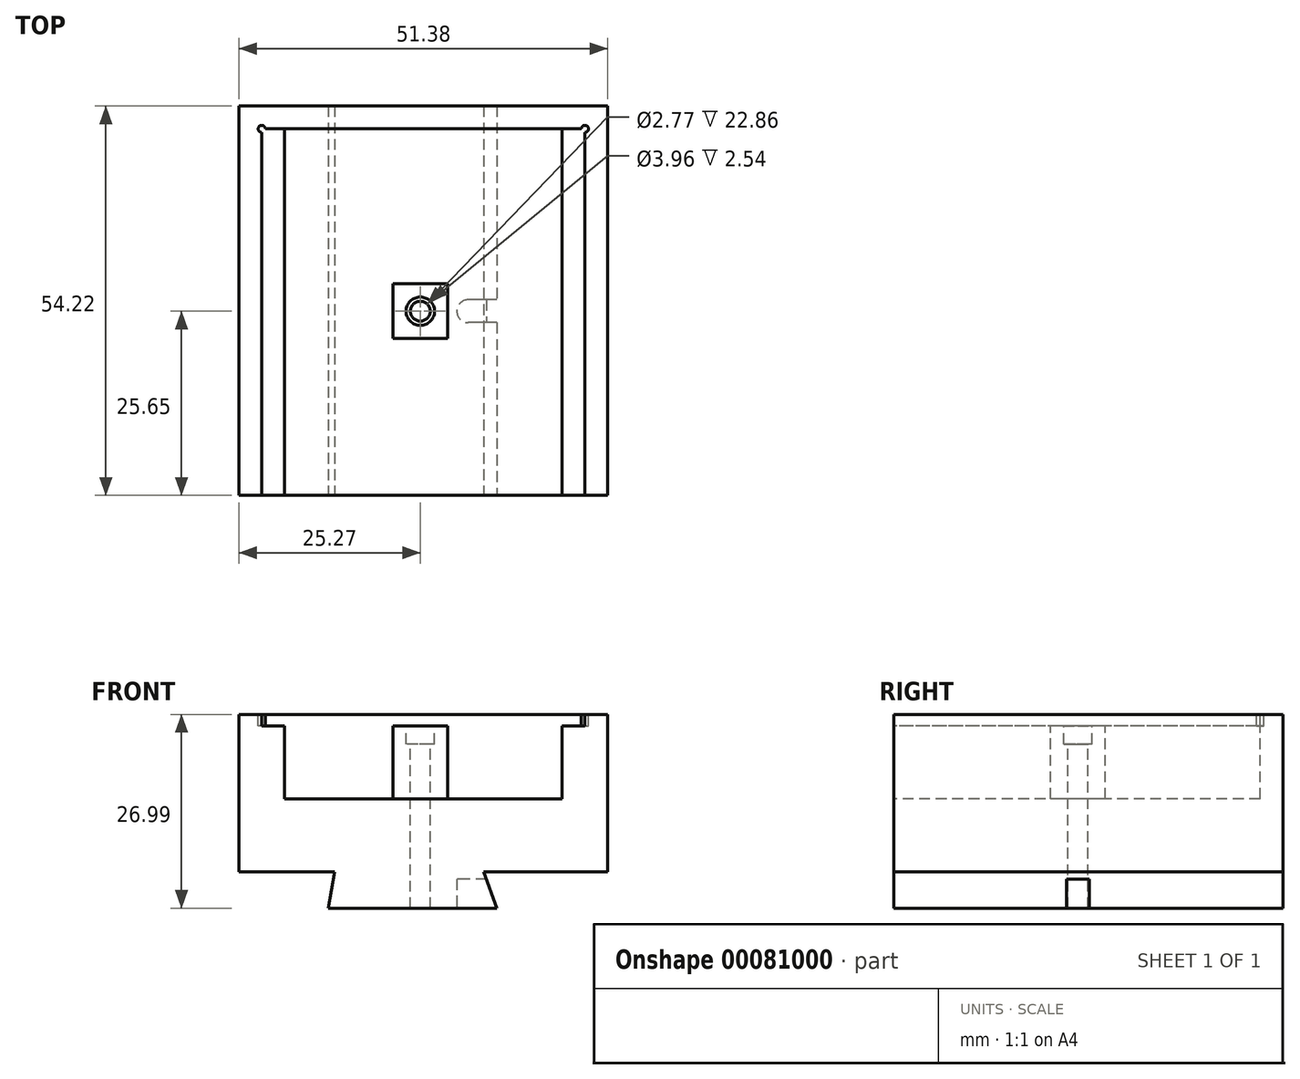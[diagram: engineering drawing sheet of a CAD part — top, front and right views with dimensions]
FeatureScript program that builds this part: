
annotation { "Feature Type Name" : "Feature", "Feature Type Description" : "" }
export const myFeature = defineFeature(function(context is Context, id is Id, definition is map)
    precondition{}
    {
        {
            var Q0;
            Q0=qCreatedBy(makeId("Top.planeOp"),FACE);
            var sketch = newSketch(context, id + "F0", { "sketchPlane" : qUnion([Q0])});
            skLineSegment(sketch, "E0.bottom", {"start": v(-25.27, 28.57) * mm, "end": v(26.11, 28.58) * mm});
            skLineSegment(sketch, "E0.top", {"start": v(-25.27, -25.65) * mm, "end": v(26.11, -25.65) * mm});
            skLineSegment(sketch, "E0.left", {"start": v(-25.27, 28.57) * mm, "end": v(-25.27, -25.65) * mm});
            skLineSegment(sketch, "E0.right", {"start": v(26.11, 28.58) * mm, "end": v(26.11, -25.65) * mm});
            skLineSegment(sketch, "E1.bottom", {"start": v(-22.1, 25.4) * mm, "end": v(22.94, 25.4) * mm});
            skLineSegment(sketch, "E1.top", {"start": v(-22.1, -25.65) * mm, "end": v(22.94, -25.65) * mm});
            skLineSegment(sketch, "E1.left", {"start": v(-22.1, 25.4) * mm, "end": v(-22.1, -25.65) * mm});
            skLineSegment(sketch, "E1.right", {"start": v(22.94, 25.4) * mm, "end": v(22.94, -25.65) * mm});
            skCircle(sketch, "E2", {"center": v(22.94, 25.4) * mm, "radius": 0.5 * mm});
            skCircle(sketch, "E3", {"center": v(-22.1, 25.4) * mm, "radius": 0.5 * mm});
            skCircle(sketch, "E4", {"center": v(0, 0) * mm, "radius": 1.38 * mm});
            skLineSegment(sketch, "E5", {"start": v(-18.92, 25.4) * mm, "end": v(-18.92, -25.65) * mm});
            skLineSegment(sketch, "E6", {"start": v(19.76, 25.4) * mm, "end": v(19.76, -25.65) * mm});
            skLineSegment(sketch, "E7.bottom", {"start": v(-3.8, 3.81) * mm, "end": v(3.81, 3.81) * mm});
            skLineSegment(sketch, "E7.top", {"start": v(-3.8, -3.81) * mm, "end": v(3.81, -3.81) * mm});
            skLineSegment(sketch, "E7.left", {"start": v(-3.81, 3.81) * mm, "end": v(-3.81, -3.81) * mm});
            skLineSegment(sketch, "E7.right", {"start": v(3.81, 3.81) * mm, "end": v(3.81, -3.81) * mm});
            skCircle(sketch, "E8", {"center": v(0, 0) * mm, "radius": 1.98 * mm});
            skSolve(sketch);
        }
        {
            var Q0;
            {var subQ5=sQuery(id+"F0.wireOp",EDGE,"E5");Q0=makeQuery(id+"F0.imprint","IMPRINT",FACE,{"disambiguationData":[TD([[makeQuery(id+"F0.imprint","IMPRINT",EDGE,{"derivedFrom":subQ5}),-1.0]])]});}
            var Q1;
            {var subQ0=sQuery(id+"F0.wireOp",EDGE,"E1.left");var subQ1=sQuery(id+"F0.wireOp",EDGE,"E1.bottom");var subQ2=makeQuery(id+"F0.imprint","INTERSECT",VERTEX,{"derivedFrom":[subQ1,subQ0]});Q1=makeQuery(id+"F0.imprint","IMPRINT",FACE,{"disambiguationData":[TD([[makeQuery(id+"F0.imprint","IMPRINT",EDGE,{"disambiguationData":[TD([[subQ2,-1.0]])],"derivedFrom":subQ1}),1.0]])]});}
            var Q2;
            {var subQ0=sQuery(id+"F0.wireOp",EDGE,"E1.left");var subQ1=sQuery(id+"F0.wireOp",EDGE,"E1.bottom");var subQ2=makeQuery(id+"F0.imprint","INTERSECT",VERTEX,{"derivedFrom":[subQ1,subQ0]});Q2=makeQuery(id+"F0.imprint","IMPRINT",FACE,{"disambiguationData":[TD([[makeQuery(id+"F0.imprint","IMPRINT",EDGE,{"disambiguationData":[TD([[subQ2,-1.0]])],"derivedFrom":subQ1}),-1.0]])]});}
            var Q3;
            {var subQ7=sQuery(id+"F0.wireOp",EDGE,"E6");Q3=makeQuery(id+"F0.imprint","IMPRINT",FACE,{"disambiguationData":[TD([[makeQuery(id+"F0.imprint","IMPRINT",EDGE,{"derivedFrom":subQ7}),1.0]])]});}
            var Q4;
            Q4=makeQuery(id+"F0.imprint","IMPRINT",FACE,{"disambiguationData":[TD([[makeQuery(id+"F0.imprint","IMPRINT",EDGE,{"derivedFrom":sQuery(id+"F0.wireOp",EDGE,"E4")}),-1.0]])]});
            var Q5;
            Q5=makeQuery(id+"F0.imprint","IMPRINT",FACE,{"disambiguationData":[TD([[makeQuery(id+"F0.imprint","IMPRINT",EDGE,{"derivedFrom":sQuery(id+"F0.wireOp",EDGE,"E0.bottom")}),-1.0]])]});
            var Q6;
            {var subQ0=sQuery(id+"F0.wireOp",EDGE,"E1.right");var subQ1=sQuery(id+"F0.wireOp",EDGE,"E1.bottom");var subQ2=makeQuery(id+"F0.imprint","INTERSECT",VERTEX,{"derivedFrom":[subQ1,subQ0]});Q6=makeQuery(id+"F0.imprint","IMPRINT",FACE,{"disambiguationData":[TD([[makeQuery(id+"F0.imprint","IMPRINT",EDGE,{"disambiguationData":[TD([[subQ2,1.0]])],"derivedFrom":subQ1}),-1.0]])]});}
            var Q7;
            {var subQ0=sQuery(id+"F0.wireOp",EDGE,"E1.right");var subQ1=sQuery(id+"F0.wireOp",EDGE,"E1.bottom");var subQ2=makeQuery(id+"F0.imprint","INTERSECT",VERTEX,{"derivedFrom":[subQ1,subQ0]});Q7=makeQuery(id+"F0.imprint","IMPRINT",FACE,{"disambiguationData":[TD([[makeQuery(id+"F0.imprint","IMPRINT",EDGE,{"disambiguationData":[TD([[subQ2,1.0]])],"derivedFrom":subQ1}),1.0]])]});}
            var Q8;
            {var subQ1=sQuery(id+"F0.wireOp",EDGE,"E5");Q8=makeQuery(id+"F0.imprint","IMPRINT",FACE,{"disambiguationData":[TD([[makeQuery(id+"F0.imprint","IMPRINT",EDGE,{"derivedFrom":subQ1}),1.0]])]});}
            var Q9;
            Q9=makeQuery(id+"F0.imprint","IMPRINT",FACE,{"disambiguationData":[TD([[makeQuery(id+"F0.imprint","IMPRINT",EDGE,{"derivedFrom":sQuery(id+"F0.wireOp",EDGE,"E7.bottom")}),-1.0]])]});
            extrude(context, id + "F1", {"entities" : qUnion([Q0, Q1, Q2, Q3, Q4, Q5, Q6, Q7, Q8, Q9]), "oppositeDirection" : true, "depth" : 26.99 * mm});
        }
        {
            var Q0;
            {var subQ5=sQuery(id+"F0.wireOp",EDGE,"E5");Q0=makeQuery(id+"F0.imprint","IMPRINT",FACE,{"disambiguationData":[TD([[makeQuery(id+"F0.imprint","IMPRINT",EDGE,{"derivedFrom":subQ5}),-1.0]])]});}
            var Q1;
            Q1=makeQuery(id+"F0.imprint","IMPRINT",FACE,{"disambiguationData":[TD([[makeQuery(id+"F0.imprint","IMPRINT",EDGE,{"derivedFrom":sQuery(id+"F0.wireOp",EDGE,"E4")}),-1.0]])]});
            var Q2;
            {var subQ7=sQuery(id+"F0.wireOp",EDGE,"E6");Q2=makeQuery(id+"F0.imprint","IMPRINT",FACE,{"disambiguationData":[TD([[makeQuery(id+"F0.imprint","IMPRINT",EDGE,{"derivedFrom":subQ7}),1.0]])]});}
            var Q3;
            {var subQ0=sQuery(id+"F0.wireOp",EDGE,"E1.right");var subQ1=sQuery(id+"F0.wireOp",EDGE,"E1.bottom");var subQ2=makeQuery(id+"F0.imprint","INTERSECT",VERTEX,{"derivedFrom":[subQ1,subQ0]});Q3=makeQuery(id+"F0.imprint","IMPRINT",FACE,{"disambiguationData":[TD([[makeQuery(id+"F0.imprint","IMPRINT",EDGE,{"disambiguationData":[TD([[subQ2,1.0]])],"derivedFrom":subQ1}),1.0]])]});}
            var Q4;
            {var subQ0=sQuery(id+"F0.wireOp",EDGE,"E1.right");var subQ1=sQuery(id+"F0.wireOp",EDGE,"E1.bottom");var subQ2=makeQuery(id+"F0.imprint","INTERSECT",VERTEX,{"derivedFrom":[subQ1,subQ0]});Q4=makeQuery(id+"F0.imprint","IMPRINT",FACE,{"disambiguationData":[TD([[makeQuery(id+"F0.imprint","IMPRINT",EDGE,{"disambiguationData":[TD([[subQ2,1.0]])],"derivedFrom":subQ1}),-1.0]])]});}
            var Q5;
            {var subQ0=sQuery(id+"F0.wireOp",EDGE,"E1.left");var subQ1=sQuery(id+"F0.wireOp",EDGE,"E1.bottom");var subQ2=makeQuery(id+"F0.imprint","INTERSECT",VERTEX,{"derivedFrom":[subQ1,subQ0]});Q5=makeQuery(id+"F0.imprint","IMPRINT",FACE,{"disambiguationData":[TD([[makeQuery(id+"F0.imprint","IMPRINT",EDGE,{"disambiguationData":[TD([[subQ2,-1.0]])],"derivedFrom":subQ1}),-1.0]])]});}
            var Q6;
            {var subQ0=sQuery(id+"F0.wireOp",EDGE,"E1.left");var subQ1=sQuery(id+"F0.wireOp",EDGE,"E1.bottom");var subQ2=makeQuery(id+"F0.imprint","INTERSECT",VERTEX,{"derivedFrom":[subQ1,subQ0]});Q6=makeQuery(id+"F0.imprint","IMPRINT",FACE,{"disambiguationData":[TD([[makeQuery(id+"F0.imprint","IMPRINT",EDGE,{"disambiguationData":[TD([[subQ2,-1.0]])],"derivedFrom":subQ1}),1.0]])]});}
            var Q7;
            {var subQ1=sQuery(id+"F0.wireOp",EDGE,"E5");Q7=makeQuery(id+"F0.imprint","IMPRINT",FACE,{"disambiguationData":[TD([[makeQuery(id+"F0.imprint","IMPRINT",EDGE,{"derivedFrom":subQ1}),1.0]])]});}
            var Q8;
            Q8=makeQuery(id+"F0.imprint","IMPRINT",FACE,{"disambiguationData":[TD([[makeQuery(id+"F0.imprint","IMPRINT",EDGE,{"derivedFrom":sQuery(id+"F0.wireOp",EDGE,"E7.bottom")}),-1.0]])]});
            extrude(context, id + "F2", {"entities" : qUnion([Q0, Q1, Q2, Q3, Q4, Q5, Q6, Q7, Q8]), "operationType" : NewBodyOperationType.REMOVE, "oppositeDirection" : true, "depth" : 1.59 * mm});
        }
        {
            var Q0;
            {var subQ1=sQuery(id+"F0.wireOp",EDGE,"E5");Q0=makeQuery(id+"F0.imprint","IMPRINT",FACE,{"disambiguationData":[TD([[makeQuery(id+"F0.imprint","IMPRINT",EDGE,{"derivedFrom":subQ1}),1.0]])]});}
            extrude(context, id + "F3", {"entities" : qUnion([Q0]), "operationType" : NewBodyOperationType.REMOVE, "oppositeDirection" : true, "depth" : 11.75 * mm});
        }
        {
            var Q0;
            Q0=makeQuery(id+"F0.imprint","IMPRINT",FACE,{"disambiguationData":[TD([[makeQuery(id+"F0.imprint","IMPRINT",EDGE,{"derivedFrom":sQuery(id+"F0.wireOp",EDGE,"E4")}),-1.0]])]});
            extrude(context, id + "F4", {"entities" : qUnion([Q0]), "operationType" : NewBodyOperationType.REMOVE, "oppositeDirection" : true, "depth" : 4.13 * mm});
        }
        {
            var Q0;
            Q0=makeQuery(id+"F1.opExtrude","SWEPT_FACE",FACE,{"disambiguationData":[OSD([sQuery(id+"F0.wireOp",EDGE,"E0.top"),sQuery(id+"F0.wireOp",EDGE,"E1.top")])]});
            var sketch = newSketch(context, id + "F5", { "sketchPlane" : qUnion([Q0])});
            skLineSegment(sketch, "E9.0.0", {"start": v(19.76, -11.75) * mm, "end": v(-18.92, -11.75) * mm});
            skLineSegment(sketch, "E9.0.1", {"start": v(-18.92, -11.75) * mm, "end": v(-18.92, -1.59) * mm});
            skLineSegment(sketch, "E9.0.2", {"start": v(-18.92, -1.59) * mm, "end": v(-22.1, -1.59) * mm});
            skLineSegment(sketch, "E9.0.3", {"start": v(-22.1, -1.59) * mm, "end": v(-22.1, 0) * mm});
            skLineSegment(sketch, "E9.0.4", {"start": v(-22.1, 0) * mm, "end": v(-25.27, 0) * mm});
            skLineSegment(sketch, "E9.0.5", {"start": v(-25.27, 0) * mm, "end": v(-25.27, -26.99) * mm});
            skLineSegment(sketch, "E9.0.6", {"start": v(-25.27, -26.99) * mm, "end": v(26.11, -26.99) * mm});
            skLineSegment(sketch, "E9.0.7", {"start": v(26.11, -26.99) * mm, "end": v(26.11, 0) * mm});
            skLineSegment(sketch, "E9.0.8", {"start": v(26.11, 0) * mm, "end": v(22.94, 0) * mm});
            skLineSegment(sketch, "E9.0.9", {"start": v(22.94, 0) * mm, "end": v(22.94, -1.59) * mm});
            skLineSegment(sketch, "E9.0.10", {"start": v(22.94, -1.59) * mm, "end": v(19.76, -1.59) * mm});
            skLineSegment(sketch, "E9.0.11", {"start": v(19.76, -1.59) * mm, "end": v(19.76, -11.75) * mm});
            skLineSegment(sketch, "E10", {"start": v(-25.27, -21.9) * mm, "end": v(-11.93, -21.9) * mm});
            skLineSegment(sketch, "E11", {"start": v(-11.93, -21.9) * mm, "end": v(-12.83, -26.99) * mm});
            skLineSegment(sketch, "E12", {"start": v(26.11, -21.9) * mm, "end": v(8.85, -21.9) * mm});
            skLineSegment(sketch, "E13", {"start": v(8.85, -21.9) * mm, "end": v(10.7, -26.99) * mm});
            skSolve(sketch);
        }
        {
            var Q0;
            {var subQ3=sQuery(id+"F5.wireOp",EDGE,"E10");Q0=makeQuery(id+"F5.imprint","IMPRINT",FACE,{"disambiguationData":[TD([[makeQuery(id+"F5.imprint","IMPRINT",EDGE,{"derivedFrom":subQ3}),-1.0]])]});}
            var Q1;
            {var subQ4=sQuery(id+"F5.wireOp",EDGE,"E12");Q1=makeQuery(id+"F5.imprint","IMPRINT",FACE,{"disambiguationData":[TD([[makeQuery(id+"F5.imprint","IMPRINT",EDGE,{"derivedFrom":subQ4}),1.0]])]});}
            extrude(context, id + "F6", {"entities" : qUnion([Q0, Q1]), "operationType" : NewBodyOperationType.REMOVE, "endBound" : BoundingType.THROUGH_ALL, "oppositeDirection" : true, "depth" : 25.4 * mm});
        }
        {
            var Q0;
            Q0=makeQuery(id+"F1.opExtrude","CAP_FACE",FACE,{"disambiguationData":[OSD([sQuery(id+"F0.wireOp",EDGE,"E0.bottom"),sQuery(id+"F0.wireOp",EDGE,"E0.top"),sQuery(id+"F0.wireOp",EDGE,"E0.left"),sQuery(id+"F0.wireOp",EDGE,"E0.right"),sQuery(id+"F0.wireOp",EDGE,"E1.top"),sQuery(id+"F0.wireOp",EDGE,"E4")])],"isStart":false});
            var sketch = newSketch(context, id + "F7", { "sketchPlane" : qUnion([Q0])});
            skCircle(sketch, "E14", {"center": v(6.67, 0) * mm, "radius": 1.59 * mm});
            skLineSegment(sketch, "E15.0.0", {"start": v(-12.83, -28.57) * mm, "end": v(10.7, -28.58) * mm});
            skLineSegment(sketch, "E15.0.1", {"start": v(10.7, -28.58) * mm, "end": v(10.7, 25.65) * mm});
            skLineSegment(sketch, "E15.0.2", {"start": v(10.7, 25.65) * mm, "end": v(-12.83, 25.65) * mm});
            skLineSegment(sketch, "E15.0.3", {"start": v(-12.83, 25.65) * mm, "end": v(-12.83, -28.57) * mm});
            skLineSegment(sketch, "E16", {"start": v(10.7, 1.59) * mm, "end": v(6.67, 1.59) * mm});
            skLineSegment(sketch, "E17", {"start": v(10.7, -1.59) * mm, "end": v(6.67, -1.59) * mm});
            skSolve(sketch);
        }
        {
            var Q0;
            {var subQ0=sQuery(id+"F7.wireOp",EDGE,"E16");Q0=makeQuery(id+"F7.imprint","IMPRINT",FACE,{"disambiguationData":[TD([[makeQuery(id+"F7.imprint","IMPRINT",EDGE,{"derivedFrom":subQ0}),1.0]])]});}
            var Q1;
            {var subQ0=sQuery(id+"F7.wireOp",EDGE,"E14");var subQ1=makeQuery(id+"F7.imprint","INTERSECT",VERTEX,{"derivedFrom":[subQ0,sQuery(id+"F7.wireOp",EDGE,"E16")]});Q1=makeQuery(id+"F7.imprint","IMPRINT",FACE,{"disambiguationData":[TD([[makeQuery(id+"F7.imprint","IMPRINT",EDGE,{"disambiguationData":[TD([[subQ1,-1.0]])],"derivedFrom":subQ0}),1.0]])]});}
            extrude(context, id + "F8", {"entities" : qUnion([Q0, Q1]), "operationType" : NewBodyOperationType.REMOVE, "oppositeDirection" : true, "depth" : 4.04 * mm});
        }
    });
